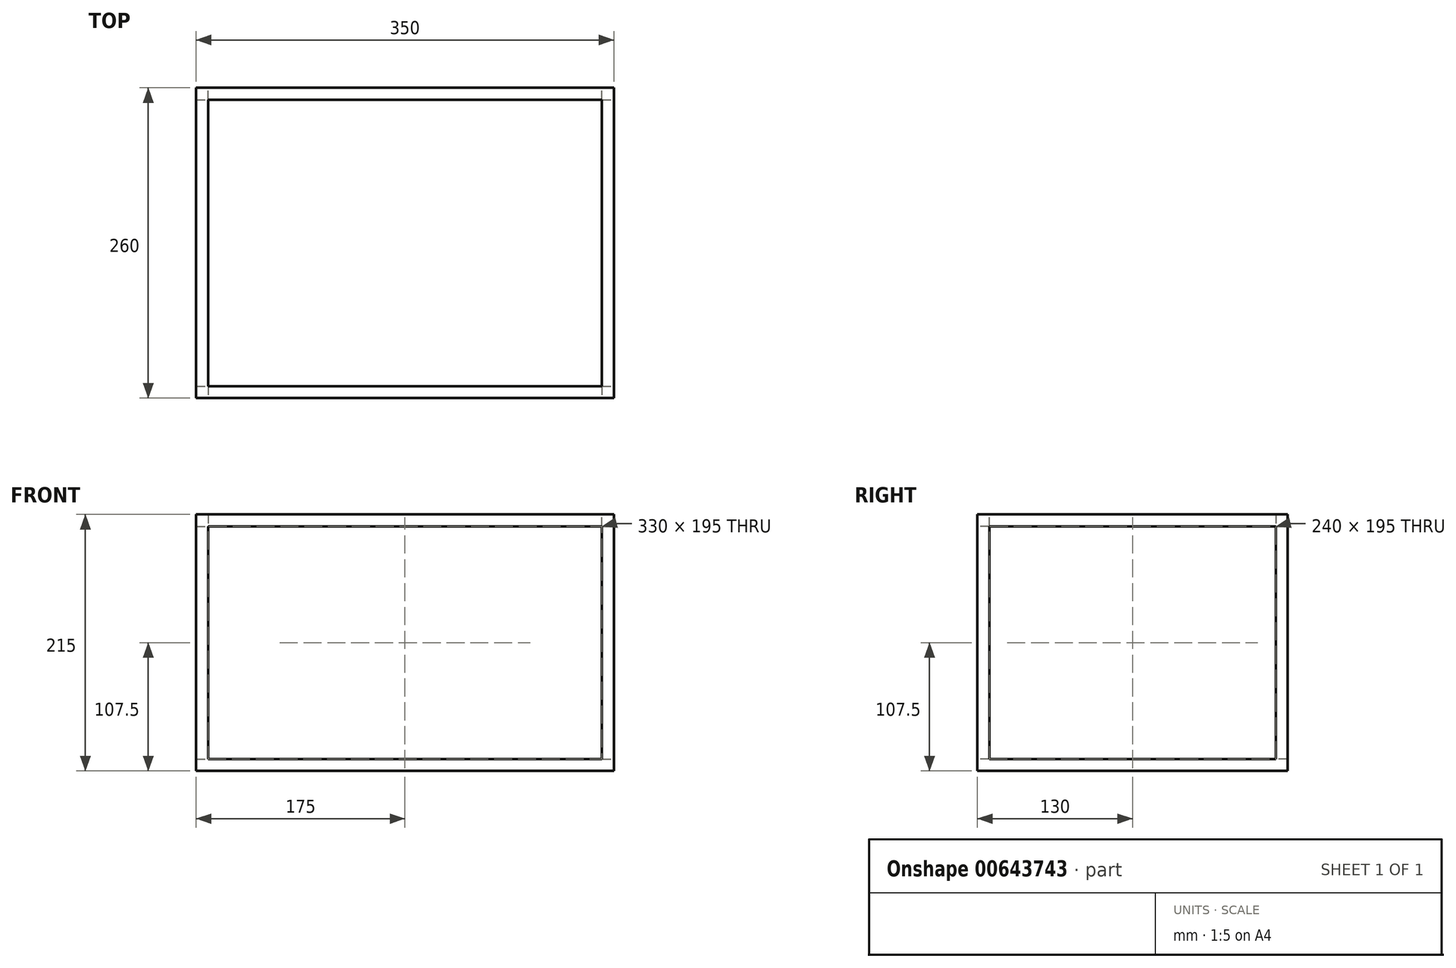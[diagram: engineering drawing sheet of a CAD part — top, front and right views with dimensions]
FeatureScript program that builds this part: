
annotation { "Feature Type Name" : "Feature", "Feature Type Description" : "" }
export const myFeature = defineFeature(function(context is Context, id is Id, definition is map)
    precondition{}
    {
        {
            var Q0;
            Q0=qCreatedBy(makeId("Front.planeOp"),FACE);
            var sketch = newSketch(context, id + "F0", { "sketchPlane" : qUnion([Q0])});
            skLineSegment(sketch, "E0.bottom", {"start": v(0, 0) * mm, "end": v(330, 0) * mm});
            skLineSegment(sketch, "E0.top", {"start": v(0, 195) * mm, "end": v(330, 195) * mm});
            skLineSegment(sketch, "E0.left", {"start": v(0, 0) * mm, "end": v(0, 195) * mm});
            skLineSegment(sketch, "E0.right", {"start": v(330, 0) * mm, "end": v(330, 195) * mm});
            skLineSegment(sketch, "E1.bottom", {"start": v(-10, -10) * mm, "end": v(340, -10) * mm});
            skLineSegment(sketch, "E1.top", {"start": v(-10, 205) * mm, "end": v(340, 205) * mm});
            skLineSegment(sketch, "E1.left", {"start": v(-10, -10) * mm, "end": v(-10, 205) * mm});
            skLineSegment(sketch, "E1.right", {"start": v(340, -10) * mm, "end": v(340, 205) * mm});
            skSolve(sketch);
        }
        {
            var Q0;
            Q0=qCreatedBy(makeId("Right.planeOp"),FACE);
            var sketch = newSketch(context, id + "F1", { "sketchPlane" : qUnion([Q0])});
            skPoint(sketch, "E2.0", {"position": v(0, 205) * mm});
            skLineSegment(sketch, "E3.bottom", {"start": v(0, 205) * mm, "end": v(260, 205) * mm});
            skLineSegment(sketch, "E3.top", {"start": v(0, -10) * mm, "end": v(260, -10) * mm});
            skLineSegment(sketch, "E3.left", {"start": v(0, 205) * mm, "end": v(0, -10) * mm});
            skLineSegment(sketch, "E3.right", {"start": v(260, 205) * mm, "end": v(260, -10) * mm});
            skLineSegment(sketch, "E4", {"start": v(10, 0) * mm, "end": v(10, 195) * mm});
            skLineSegment(sketch, "E5", {"start": v(10, 195) * mm, "end": v(250, 195) * mm});
            skLineSegment(sketch, "E6", {"start": v(250, 195) * mm, "end": v(250, 0) * mm});
            skLineSegment(sketch, "E7", {"start": v(250, 0) * mm, "end": v(10, 0) * mm});
            skSolve(sketch);
        }
        {
            var Q0;
            Q0=makeQuery(id+"F0.imprint","IMPRINT",FACE,{"disambiguationData":[TD([[makeQuery(id+"F0.imprint","IMPRINT",EDGE,{"derivedFrom":sQuery(id+"F0.wireOp",EDGE,"E0.bottom")}),-1.0]])]});
            var Q1;
            Q1=sQuery(id+"F1.wireOp",VERTEX,"E5.start");
            extrude(context, id + "F2", {"entities" : qUnion([Q0]), "endBound" : BoundingType.UP_TO_VERTEX, "oppositeDirection" : true, "depth" : 25 * mm, "endBoundEntityVertex" : qUnion([Q1]), "offsetDistance" : 25 * mm});
        }
        {
            var Q0;
            Q0=makeQuery(id+"F1.imprint","IMPRINT",FACE,{"disambiguationData":[TD([[makeQuery(id+"F1.imprint","IMPRINT",EDGE,{"derivedFrom":sQuery(id+"F1.wireOp",EDGE,"E3.bottom")}),-1.0]])]});
            var Q1;
            Q1=makeQuery(id+"F2.opExtrude","CAP_VERTEX",VERTEX,{"disambiguationData":[OSD([sQuery(id+"F0.wireOp",EDGE,"E1.top"),sQuery(id+"F0.wireOp",EDGE,"E1.left")])],"isStart":false});
            extrude(context, id + "F3", {"entities" : qUnion([Q0]), "operationType" : NewBodyOperationType.ADD, "endBound" : BoundingType.UP_TO_VERTEX, "oppositeDirection" : true, "depth" : 25 * mm, "endBoundEntityVertex" : qUnion([Q1]), "offsetDistance" : 25 * mm});
        }
        {
            var Q0;
            Q0=makeQuery(id+"F3.boolean.opBoolean","MERGE",FACE,{"derivedFrom":[makeQuery(id+"F2.opExtrude","SWEPT_FACE",FACE,{"disambiguationData":[OSD([sQuery(id+"F0.wireOp",EDGE,"E1.bottom")])]}),makeQuery(id+"F3.opExtrude","SWEPT_FACE",FACE,{"disambiguationData":[OSD([sQuery(id+"F1.wireOp",EDGE,"E3.top")])]})]});
            var sketch = newSketch(context, id + "F4", { "sketchPlane" : qUnion([Q0])});
            skPoint(sketch, "E8.0", {"position": v(-10, 0) * mm});
            skPoint(sketch, "E9.0", {"position": v(340, 0) * mm});
            skPoint(sketch, "E10.0", {"position": v(-10, -260) * mm});
            skLineSegment(sketch, "E11.bottom", {"start": v(340, 0) * mm, "end": v(-10, 0) * mm});
            skLineSegment(sketch, "E11.top", {"start": v(340, -260) * mm, "end": v(-10, -260) * mm});
            skLineSegment(sketch, "E11.left", {"start": v(340, 0) * mm, "end": v(340, -260) * mm});
            skLineSegment(sketch, "E11.right", {"start": v(-10, 0) * mm, "end": v(-10, -260) * mm});
            skSolve(sketch);
        }
        {
            var Q0;
            {var subQ1=sQuery(id+"F4.wireOp",EDGE,"E11.bottom");Q0=makeQuery(id+"F4.imprint","IMPRINT",FACE,{"disambiguationData":[TD([[makeQuery(id+"F4.imprint","IMPRINT",EDGE,{"derivedFrom":subQ1}),-1.0]])]});}
            var Q1;
            {var subQ4=makeQuery(id+"F2.opExtrude","CAP_EDGE",EDGE,{"disambiguationData":[OSD([sQuery(id+"F0.wireOp",EDGE,"E1.bottom")])],"isStart":false});Q1=makeQuery(id+"F4.imprint","IMPRINT",FACE,{"disambiguationData":[TD([[makeQuery(id+"F4.imprint","IMPRINT",EDGE,{"derivedFrom":subQ4}),-1.0]])]});}
            var Q2;
            Q2=makeQuery(id+"F2.opExtrude","CAP_VERTEX",VERTEX,{"disambiguationData":[OSD([sQuery(id+"F0.wireOp",EDGE,"E0.bottom"),sQuery(id+"F0.wireOp",EDGE,"E0.right")])],"isStart":false});
            extrude(context, id + "F5", {"entities" : qUnion([Q0, Q1]), "operationType" : NewBodyOperationType.ADD, "endBound" : BoundingType.UP_TO_VERTEX, "oppositeDirection" : true, "depth" : 10 * mm, "endBoundEntityVertex" : qUnion([Q2]), "offsetDistance" : 25 * mm});
        }
        {
            var Q0;
            Q0=qCreatedBy(makeId("Front.planeOp"),FACE);
            var Q1;
            Q1=makeQuery(id+"F5.boolean.opBoolean","INTERSECT",VERTEX,{"derivedFrom":[makeQuery(id+"F3.opExtrude","CAP_FACE",FACE,{"disambiguationData":[OSD([sQuery(id+"F1.wireOp",EDGE,"E3.bottom"),sQuery(id+"F1.wireOp",EDGE,"E3.top"),sQuery(id+"F1.wireOp",EDGE,"E3.left"),sQuery(id+"F1.wireOp",EDGE,"E3.right"),sQuery(id+"F1.wireOp",EDGE,"E4"),sQuery(id+"F1.wireOp",EDGE,"E5"),sQuery(id+"F1.wireOp",EDGE,"E6"),sQuery(id+"F1.wireOp",EDGE,"E7")])],"isStart":true}),makeQuery(id+"F5.opExtrude","CAP_FACE",FACE,{"disambiguationData":[OSD([sQuery(id+"F4.wireOp",EDGE,"E11.bottom"),sQuery(id+"F4.wireOp",EDGE,"E11.top"),sQuery(id+"F4.wireOp",EDGE,"E11.left"),sQuery(id+"F4.wireOp",EDGE,"E11.right")])],"isStart":false})]});
            cPlane(context, id + "F6", {"entities" : qUnion([Q0, Q1]), "cplaneType" : CPlaneType.PLANE_POINT, "offset" : 25 * mm, "width" : 150 * mm, "height" : 150 * mm});
        }
        {
            var Q0;
            Q0=qCreatedBy(makeId("Right.planeOp"),FACE);
            var Q1;
            {var subQ1=sQuery(id+"F0.wireOp",EDGE,"E0.left");var subQ2=sQuery(id+"F0.wireOp",EDGE,"E1.right");var subQ3=sQuery(id+"F0.wireOp",EDGE,"E1.top");var subQ5=sQuery(id+"F0.wireOp",EDGE,"E1.bottom");var subQ6=sQuery(id+"F0.wireOp",EDGE,"E0.right");var subQ9=sQuery(id+"F0.wireOp",EDGE,"E0.bottom");var subQ10=sQuery(id+"F0.wireOp",EDGE,"E0.top");var subQ11=makeQuery(id+"F2.opExtrude","CAP_FACE",FACE,{"disambiguationData":[OSD([subQ9,subQ10,subQ1,subQ6,subQ5,subQ3,sQuery(id+"F0.wireOp",EDGE,"E1.left"),subQ2])],"isStart":false});Q1=makeQuery(id+"F5.boolean.opBoolean","INTERSECT",VERTEX,{"derivedFrom":[makeQuery(id+"F3.boolean.opBoolean","SPLIT",FACE,{"disambiguationData":[TD([makeQuery(id+"F2.opExtrude","SWEPT_FACE",FACE,{"disambiguationData":[OSD([subQ6])]})])],"derivedFrom":subQ11}),makeQuery(id+"F5.opExtrude","CAP_FACE",FACE,{"disambiguationData":[OSD([sQuery(id+"F4.wireOp",EDGE,"E11.bottom"),sQuery(id+"F4.wireOp",EDGE,"E11.top"),sQuery(id+"F4.wireOp",EDGE,"E11.left"),sQuery(id+"F4.wireOp",EDGE,"E11.right")])],"isStart":false})]});}
            cPlane(context, id + "F7", {"entities" : qUnion([Q0, Q1]), "cplaneType" : CPlaneType.PLANE_POINT, "offset" : 25 * mm, "width" : 150 * mm, "height" : 150 * mm});
        }
        {
            var Q0;
            Q0=qCreatedBy(id+"F6.planeOp",FACE);
            var sketch = newSketch(context, id + "F8", { "sketchPlane" : qUnion([Q0])});
            skLineSegment(sketch, "E12.bottom", {"start": v(0, 0) * mm, "end": v(330, 0) * mm});
            skLineSegment(sketch, "E12.top", {"start": v(0, 195) * mm, "end": v(330, 195) * mm});
            skLineSegment(sketch, "E12.left", {"start": v(0, 0) * mm, "end": v(0, 195) * mm});
            skLineSegment(sketch, "E12.right", {"start": v(330, 0) * mm, "end": v(330, 195) * mm});
            skLineSegment(sketch, "E13.bottom", {"start": v(-10, -10) * mm, "end": v(340, -10) * mm});
            skLineSegment(sketch, "E13.top", {"start": v(-10, 205) * mm, "end": v(340, 205) * mm});
            skLineSegment(sketch, "E13.left", {"start": v(-10, -10) * mm, "end": v(-10, 205) * mm});
            skLineSegment(sketch, "E13.right", {"start": v(340, -10) * mm, "end": v(340, 205) * mm});
            skSolve(sketch);
        }
        {
            var Q0;
            Q0=qCreatedBy(id+"F7.planeOp",FACE);
            var sketch = newSketch(context, id + "F9", { "sketchPlane" : qUnion([Q0])});
            skPoint(sketch, "E14.0", {"position": v(0, 205) * mm});
            skLineSegment(sketch, "E15.bottom", {"start": v(0, 205) * mm, "end": v(260, 205) * mm});
            skLineSegment(sketch, "E15.top", {"start": v(0, -10) * mm, "end": v(260, -10) * mm});
            skLineSegment(sketch, "E15.left", {"start": v(0, 205) * mm, "end": v(0, -10) * mm});
            skLineSegment(sketch, "E15.right", {"start": v(260, 205) * mm, "end": v(260, -10) * mm});
            skLineSegment(sketch, "E16", {"start": v(10, 0) * mm, "end": v(10, 195) * mm});
            skLineSegment(sketch, "E17", {"start": v(10, 195) * mm, "end": v(250, 195) * mm});
            skLineSegment(sketch, "E18", {"start": v(250, 195) * mm, "end": v(250, 0) * mm});
            skLineSegment(sketch, "E19", {"start": v(250, 0) * mm, "end": v(10, 0) * mm});
            skSolve(sketch);
        }
        {
            var Q0;
            Q0=makeQuery(id+"F8.imprint","IMPRINT",FACE,{"disambiguationData":[TD([[makeQuery(id+"F8.imprint","IMPRINT",EDGE,{"derivedFrom":sQuery(id+"F8.wireOp",EDGE,"E12.bottom")}),-1.0]])]});
            var Q1;
            Q1=makeQuery(id+"F3.opExtrude","CAP_VERTEX",VERTEX,{"disambiguationData":[OSD([sQuery(id+"F1.wireOp",EDGE,"E5"),sQuery(id+"F1.wireOp",EDGE,"E6")])],"isStart":true});
            extrude(context, id + "F10", {"entities" : qUnion([Q0]), "operationType" : NewBodyOperationType.ADD, "endBound" : BoundingType.UP_TO_VERTEX, "depth" : 25 * mm, "endBoundEntityVertex" : qUnion([Q1]), "offsetDistance" : 25 * mm});
        }
        {
            var Q0;
            Q0=makeQuery(id+"F9.imprint","IMPRINT",FACE,{"disambiguationData":[TD([[makeQuery(id+"F9.imprint","IMPRINT",EDGE,{"derivedFrom":sQuery(id+"F9.wireOp",EDGE,"E15.bottom")}),-1.0]])]});
            var Q1;
            Q1=makeQuery(id+"F10.opExtrude","CAP_VERTEX",VERTEX,{"disambiguationData":[OSD([sQuery(id+"F8.wireOp",EDGE,"E12.top"),sQuery(id+"F8.wireOp",EDGE,"E12.right")])],"isStart":false});
            extrude(context, id + "F11", {"entities" : qUnion([Q0]), "operationType" : NewBodyOperationType.ADD, "endBound" : BoundingType.UP_TO_VERTEX, "oppositeDirection" : true, "depth" : 25 * mm, "endBoundEntityVertex" : qUnion([Q1]), "offsetDistance" : 25 * mm});
        }
    });
